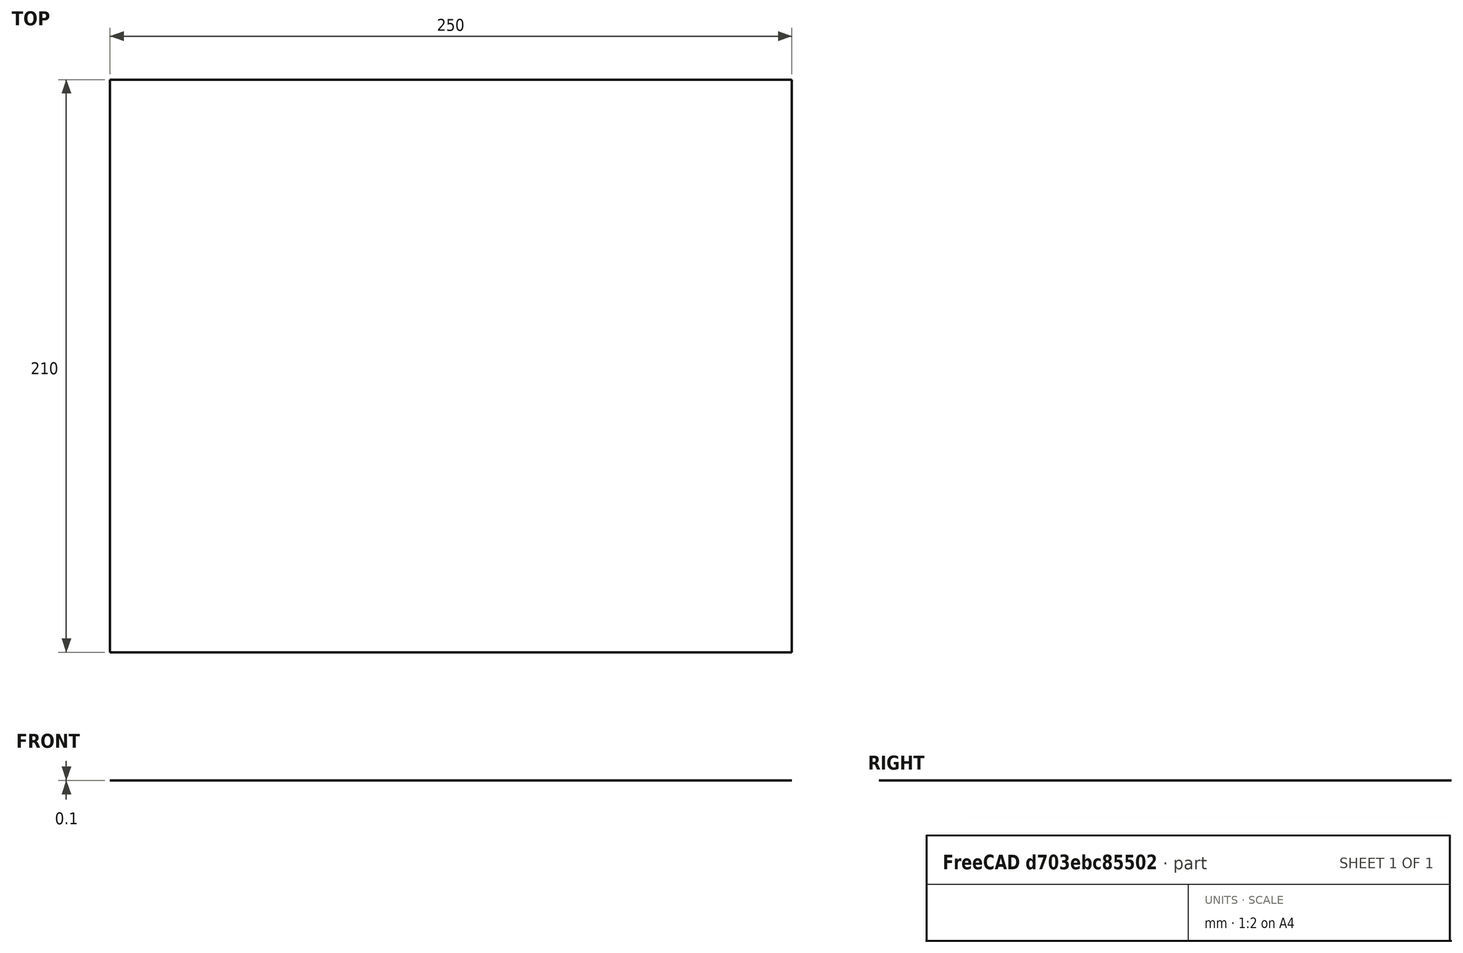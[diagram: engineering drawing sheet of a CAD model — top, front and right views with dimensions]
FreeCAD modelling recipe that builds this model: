
FCSTD DOCUMENT  (FreeCAD 1.0R39109 (Git))
Label: Printer Bed
License: Creative Commons Attribution 4.0
LicenseURL: https://creativecommons.org/licenses/by/4.0/
objects: Sketcher::SketchObject×1, PartDesign::Pad×1, PartDesign::Body×1, App::Part×1
note: 6 computed .brp shape members not serialized (recipe doc carries the construction recipe); baked Part::Feature solids carry a one-line shape summary decoded from their .brp

FEATURE [Sketcher::SketchObject] Sketch
  ArcFitTolerance = 0
  AttachmentSupport = -> [XY_Plane]
  FullyConstrained = true
  MakeInternals = false
  MapMode = 5
  sketch-geometry (5):
    g0: LineSegment StartX=-125 StartY=-105 StartZ=0 EndX=125 EndY=-105 EndZ=0
    g1: LineSegment StartX=125 StartY=-105 StartZ=0 EndX=125 EndY=105 EndZ=0
    g2: LineSegment StartX=125 StartY=105 StartZ=0 EndX=-125 EndY=105 EndZ=0
    g3: LineSegment StartX=-125 StartY=105 StartZ=0 EndX=-125 EndY=-105 EndZ=0
    g4: GeomPoint [constr] X=0 Y=0 Z=0
  constraints (12):
    c: Coincident(g0,g1)
    c: Coincident(g1,g2)
    c: Coincident(g2,g3)
    c: Coincident(g3,g0)
    c: Horizontal(g0)
    c: Horizontal(g2)
    c: Vertical(g1)
    c: Vertical(g3)
    c: Symmetric(g2,g0,g4)
    c: Distance(g1,g3) = 250
    c: Distance(g0,g2) = 210
    c: Coincident(g4,g-1)
FEATURE [PartDesign::Pad] Pad
  Direction = (0,0,1)
  Length = 0.1
  Length2 = 10
  Profile = -> Sketch
  ReferenceAxis = -> Sketch [N_Axis]
  Suppressed = false
  Type = 0
FEATURE [PartDesign::Body] Body
  AllowCompound = false
  Group = -> [Sketch,Pad]
  Origin = -> Origin
  Tip = -> Pad
FEATURE [App::Part] Part  label="Printer Bed Part"
  Group = -> [Body]
  Origin = -> Origin001
